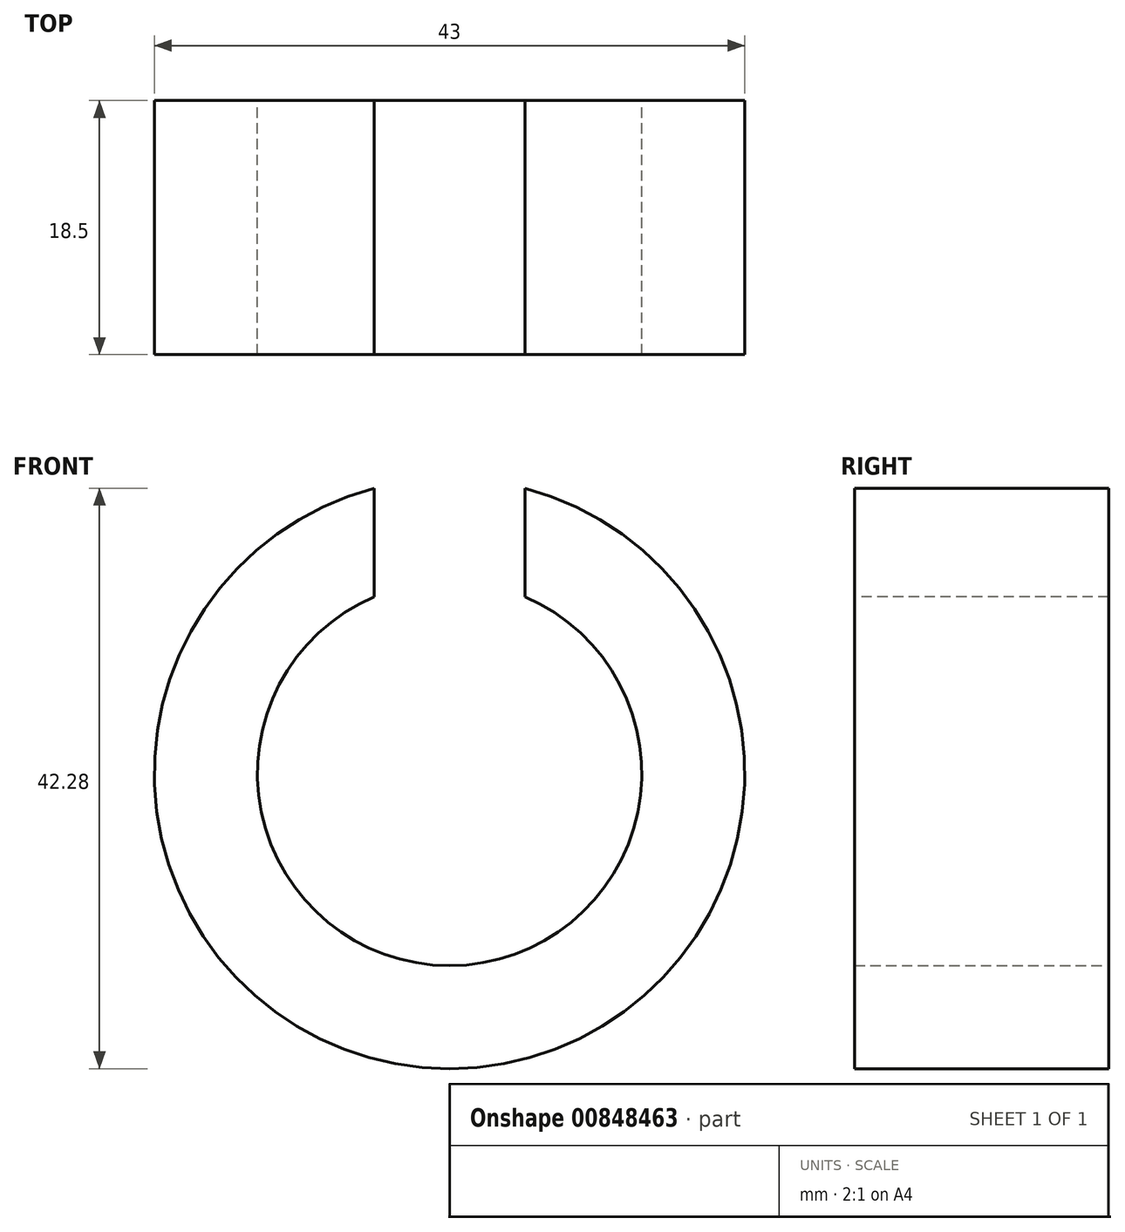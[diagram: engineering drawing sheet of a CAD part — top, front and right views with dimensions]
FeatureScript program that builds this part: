
annotation { "Feature Type Name" : "Feature", "Feature Type Description" : "" }
export const myFeature = defineFeature(function(context is Context, id is Id, definition is map)
    precondition{}
    {
        {
            var Q0;
            Q0=qCreatedBy(makeId("Front.planeOp"),FACE);
            var sketch = newSketch(context, id + "F0", { "sketchPlane" : qUnion([Q0])});
            skCircle(sketch, "E0", {"center": v(0, 0) * mm, "radius": 21.5 * mm});
            skCircle(sketch, "E1", {"center": v(0, 0) * mm, "radius": 14 * mm});
            skSolve(sketch);
        }
        {
            var Q0;
            Q0=makeQuery(id+"F0.imprint","IMPRINT",FACE,{"disambiguationData":[TD([[makeQuery(id+"F0.imprint","IMPRINT",EDGE,{"derivedFrom":sQuery(id+"F0.wireOp",EDGE,"E0")}),1.0]])]});
            var sketch = newSketch(context, id + "F1", { "sketchPlane" : qUnion([Q0])});
            skSolve(sketch);
        }
        {
            var Q0;
            Q0 = qSketchRegion(id + "F1", true);
            var Q1;
            Q1=makeQuery(id+"F1.imprint","IMPRINT",FACE,{"disambiguationData":[TD([[makeQuery(id+"F1.imprint","IMPRINT",EDGE,{"derivedFrom":makeQuery(id+"F0.imprint","IMPRINT",EDGE,{"derivedFrom":sQuery(id+"F0.wireOp",EDGE,"E0")})}),1.0]])]});
            extrude(context, id + "F2", {"entities" : qUnion([Q0, Q1]), "endBound" : BoundingType.SYMMETRIC, "depth" : 18.5 * mm, "offsetDistance" : 25.4 * mm});
        }
        {
            var Q0;
            Q0=makeQuery(id+"F2.opExtrude","CAP_FACE",FACE,{"disambiguationData":[OSD([sQuery(id+"F0.wireOp",EDGE,"E0"),sQuery(id+"F0.wireOp",EDGE,"E1")])],"isStart":false});
            var sketch = newSketch(context, id + "F3", { "sketchPlane" : qUnion([Q0])});
            skLineSegment(sketch, "E2", {"start": v(0, 21.5) * mm, "end": v(-5.5, 21.5) * mm});
            skLineSegment(sketch, "E3", {"start": v(0, 21.5) * mm, "end": v(5.5, 21.5) * mm});
            skLineSegment(sketch, "E4", {"start": v(-5.5, 21.5) * mm, "end": v(-5.5, 12.87) * mm});
            skLineSegment(sketch, "E5", {"start": v(-5.5, 12.87) * mm, "end": v(5.5, 12.87) * mm});
            skLineSegment(sketch, "E6", {"start": v(5.5, 12.87) * mm, "end": v(5.5, 21.5) * mm});
            skSolve(sketch);
        }
        {
            var Q0;
            Q0 = qSketchRegion(id + "F3", true);
            extrude(context, id + "F4", {"entities" : qUnion([Q0]), "operationType" : NewBodyOperationType.REMOVE, "oppositeDirection" : true, "depth" : 25.4 * mm, "offsetDistance" : 25.4 * mm});
        }
    });
